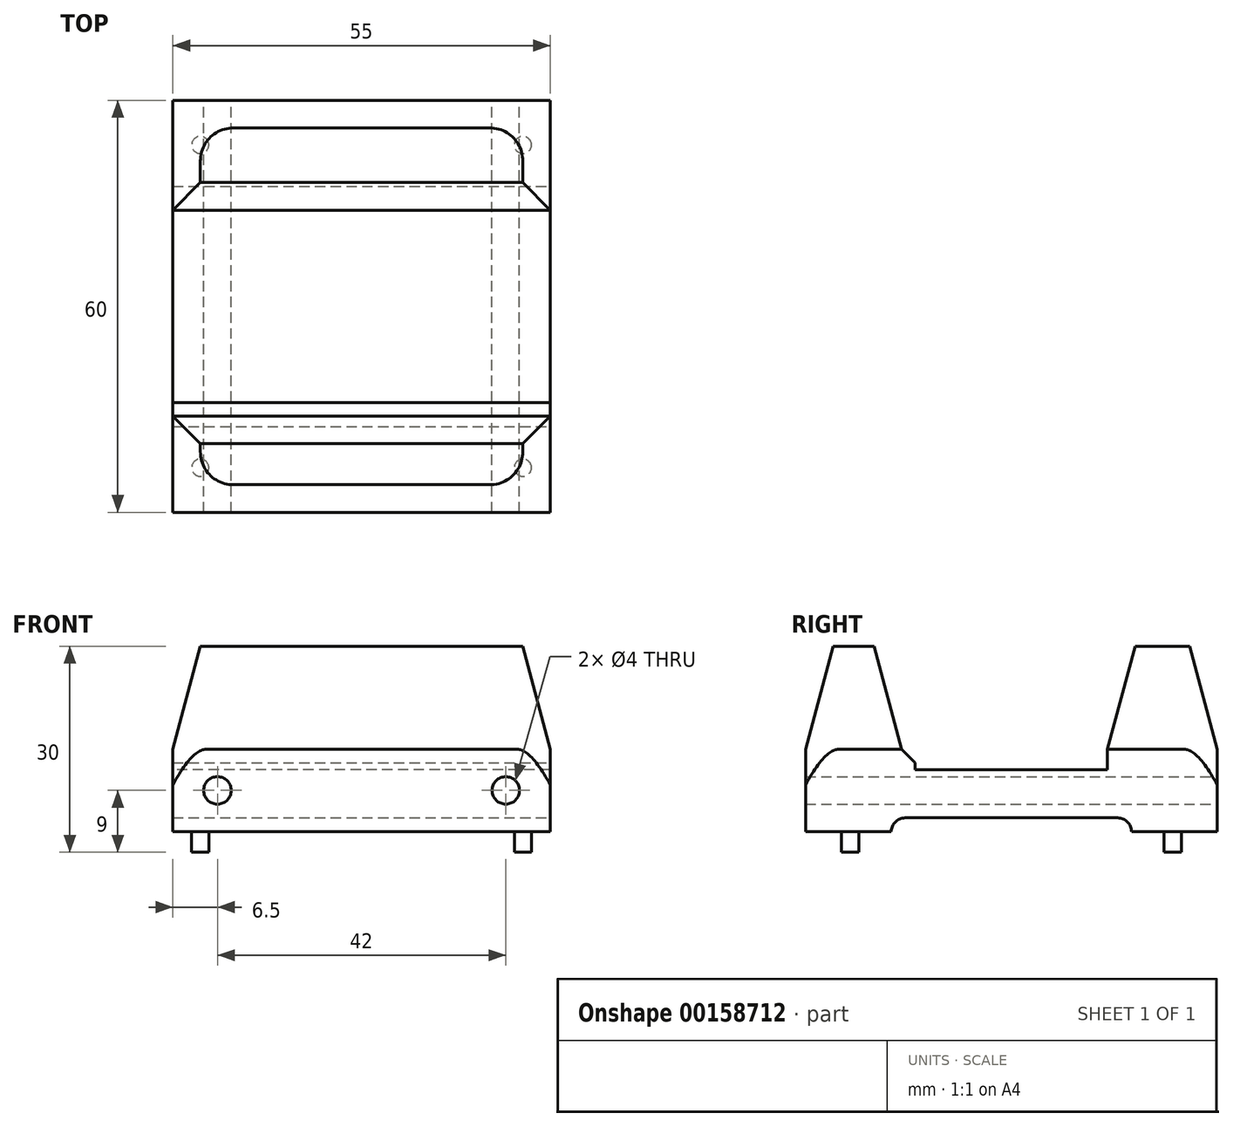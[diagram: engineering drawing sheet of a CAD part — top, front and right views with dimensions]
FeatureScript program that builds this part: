
annotation { "Feature Type Name" : "Feature", "Feature Type Description" : "" }
export const myFeature = defineFeature(function(context is Context, id is Id, definition is map)
    precondition{}
    {
        {
            var Q0;
            Q0=qCreatedBy(makeId("Top.planeOp"),FACE);
            var sketch = newSketch(context, id + "F0", { "sketchPlane" : qUnion([Q0])});
            skLineSegment(sketch, "E0.bottom", {"start": v(-23.5, 23.5) * mm, "end": v(23.5, 23.5) * mm});
            skLineSegment(sketch, "E0.top", {"start": v(-23.5, -23.5) * mm, "end": v(23.5, -23.5) * mm});
            skLineSegment(sketch, "E0.left", {"start": v(-23.5, 23.5) * mm, "end": v(-23.5, -23.5) * mm});
            skLineSegment(sketch, "E0.right", {"start": v(23.5, 23.5) * mm, "end": v(23.5, -23.5) * mm});
            skLineSegment(sketch, "E1", {"start": v(-23.5, 23.5) * mm, "end": v(23.5, -23.5) * mm, "construction": true});
            skLineSegment(sketch, "E2", {"start": v(-23.5, -23.5) * mm, "end": v(23.5, 23.5) * mm, "construction": true});
            skCircle(sketch, "E3", {"center": v(23.5, 23.5) * mm, "radius": 1.25 * mm});
            skCircle(sketch, "E4", {"center": v(23.5, -23.5) * mm, "radius": 1.25 * mm});
            skCircle(sketch, "E5", {"center": v(-23.5, -23.5) * mm, "radius": 1.25 * mm});
            skCircle(sketch, "E6", {"center": v(-23.5, 23.5) * mm, "radius": 1.25 * mm});
            skLineSegment(sketch, "E7.bottom", {"start": v(-27.5, 30) * mm, "end": v(27.5, 30) * mm});
            skLineSegment(sketch, "E7.top", {"start": v(-27.5, -30) * mm, "end": v(27.5, -30) * mm});
            skLineSegment(sketch, "E7.left", {"start": v(-27.5, 30) * mm, "end": v(-27.5, -30) * mm});
            skLineSegment(sketch, "E7.right", {"start": v(27.5, 30) * mm, "end": v(27.5, -30) * mm});
            skSolve(sketch);
        }
        {
            var Q0;
            Q0 = qSketchRegion(id + "F0", true);
            var Q1;
            {var subQ5=sQuery(id+"F0.wireOp",EDGE,"E6");var subQ13=sQuery(id+"F0.wireOp",EDGE,"E0.bottom");var subQ14=makeQuery(id+"F0.imprint","INTERSECT",VERTEX,{"derivedFrom":[subQ13,subQ5]});Q1=makeQuery(id+"F0.imprint","IMPRINT",FACE,{"disambiguationData":[TD([[makeQuery(id+"F0.imprint","IMPRINT",EDGE,{"disambiguationData":[TD([[subQ14,-1.0]])],"derivedFrom":subQ13}),-1.0]])]});}
            var Q2;
            {var subQ0=sQuery(id+"F0.wireOp",EDGE,"E0.left");var subQ1=sQuery(id+"F0.wireOp",EDGE,"E0.bottom");var subQ2=makeQuery(id+"F0.imprint","INTERSECT",VERTEX,{"derivedFrom":[subQ1,subQ0]});Q2=makeQuery(id+"F0.imprint","IMPRINT",FACE,{"disambiguationData":[TD([[makeQuery(id+"F0.imprint","IMPRINT",EDGE,{"disambiguationData":[TD([[subQ2,-1.0]])],"derivedFrom":subQ1}),1.0]])]});}
            var Q3;
            {var subQ0=sQuery(id+"F0.wireOp",EDGE,"E0.left");var subQ1=sQuery(id+"F0.wireOp",EDGE,"E0.bottom");var subQ2=makeQuery(id+"F0.imprint","INTERSECT",VERTEX,{"derivedFrom":[subQ1,subQ0]});Q3=makeQuery(id+"F0.imprint","IMPRINT",FACE,{"disambiguationData":[TD([[makeQuery(id+"F0.imprint","IMPRINT",EDGE,{"disambiguationData":[TD([[subQ2,-1.0]])],"derivedFrom":subQ1}),-1.0]])]});}
            var Q4;
            {var subQ0=sQuery(id+"F0.wireOp",EDGE,"E0.right");var subQ1=sQuery(id+"F0.wireOp",EDGE,"E0.bottom");var subQ2=makeQuery(id+"F0.imprint","INTERSECT",VERTEX,{"derivedFrom":[subQ1,subQ0]});Q4=makeQuery(id+"F0.imprint","IMPRINT",FACE,{"disambiguationData":[TD([[makeQuery(id+"F0.imprint","IMPRINT",EDGE,{"disambiguationData":[TD([[subQ2,1.0]])],"derivedFrom":subQ1}),1.0]])]});}
            var Q5;
            {var subQ0=sQuery(id+"F0.wireOp",EDGE,"E0.right");var subQ1=sQuery(id+"F0.wireOp",EDGE,"E0.bottom");var subQ2=makeQuery(id+"F0.imprint","INTERSECT",VERTEX,{"derivedFrom":[subQ1,subQ0]});Q5=makeQuery(id+"F0.imprint","IMPRINT",FACE,{"disambiguationData":[TD([[makeQuery(id+"F0.imprint","IMPRINT",EDGE,{"disambiguationData":[TD([[subQ2,1.0]])],"derivedFrom":subQ1}),-1.0]])]});}
            var Q6;
            {var subQ0=sQuery(id+"F0.wireOp",EDGE,"E0.right");var subQ1=sQuery(id+"F0.wireOp",EDGE,"E0.top");var subQ2=makeQuery(id+"F0.imprint","INTERSECT",VERTEX,{"derivedFrom":[subQ1,subQ0]});Q6=makeQuery(id+"F0.imprint","IMPRINT",FACE,{"disambiguationData":[TD([[makeQuery(id+"F0.imprint","IMPRINT",EDGE,{"disambiguationData":[TD([[subQ2,1.0]])],"derivedFrom":subQ1}),-1.0]])]});}
            var Q7;
            {var subQ0=sQuery(id+"F0.wireOp",EDGE,"E0.right");var subQ1=sQuery(id+"F0.wireOp",EDGE,"E0.top");var subQ2=makeQuery(id+"F0.imprint","INTERSECT",VERTEX,{"derivedFrom":[subQ1,subQ0]});Q7=makeQuery(id+"F0.imprint","IMPRINT",FACE,{"disambiguationData":[TD([[makeQuery(id+"F0.imprint","IMPRINT",EDGE,{"disambiguationData":[TD([[subQ2,1.0]])],"derivedFrom":subQ1}),1.0]])]});}
            var Q8;
            {var subQ0=sQuery(id+"F0.wireOp",EDGE,"E0.left");var subQ1=sQuery(id+"F0.wireOp",EDGE,"E0.top");var subQ2=makeQuery(id+"F0.imprint","INTERSECT",VERTEX,{"derivedFrom":[subQ1,subQ0]});Q8=makeQuery(id+"F0.imprint","IMPRINT",FACE,{"disambiguationData":[TD([[makeQuery(id+"F0.imprint","IMPRINT",EDGE,{"disambiguationData":[TD([[subQ2,-1.0]])],"derivedFrom":subQ1}),-1.0]])]});}
            var Q9;
            {var subQ0=sQuery(id+"F0.wireOp",EDGE,"E0.left");var subQ1=sQuery(id+"F0.wireOp",EDGE,"E0.top");var subQ2=makeQuery(id+"F0.imprint","INTERSECT",VERTEX,{"derivedFrom":[subQ1,subQ0]});Q9=makeQuery(id+"F0.imprint","IMPRINT",FACE,{"disambiguationData":[TD([[makeQuery(id+"F0.imprint","IMPRINT",EDGE,{"disambiguationData":[TD([[subQ2,-1.0]])],"derivedFrom":subQ1}),1.0]])]});}
            extrude(context, id + "F1", {"entities" : qUnion([Q0, Q1, Q2, Q3, Q4, Q5, Q6, Q7, Q8, Q9]), "depth" : 12 * mm});
        }
        {
            var Q0;
            {var subQ0=sQuery(id+"F0.wireOp",EDGE,"E0.left");var subQ1=sQuery(id+"F0.wireOp",EDGE,"E0.bottom");var subQ2=makeQuery(id+"F0.imprint","INTERSECT",VERTEX,{"derivedFrom":[subQ1,subQ0]});Q0=makeQuery(id+"F0.imprint","IMPRINT",FACE,{"disambiguationData":[TD([[makeQuery(id+"F0.imprint","IMPRINT",EDGE,{"disambiguationData":[TD([[subQ2,-1.0]])],"derivedFrom":subQ1}),1.0]])]});}
            var Q1;
            {var subQ0=sQuery(id+"F0.wireOp",EDGE,"E0.left");var subQ1=sQuery(id+"F0.wireOp",EDGE,"E0.bottom");var subQ2=makeQuery(id+"F0.imprint","INTERSECT",VERTEX,{"derivedFrom":[subQ1,subQ0]});Q1=makeQuery(id+"F0.imprint","IMPRINT",FACE,{"disambiguationData":[TD([[makeQuery(id+"F0.imprint","IMPRINT",EDGE,{"disambiguationData":[TD([[subQ2,-1.0]])],"derivedFrom":subQ1}),-1.0]])]});}
            var Q2;
            {var subQ0=sQuery(id+"F0.wireOp",EDGE,"E0.left");var subQ1=sQuery(id+"F0.wireOp",EDGE,"E0.top");var subQ2=makeQuery(id+"F0.imprint","INTERSECT",VERTEX,{"derivedFrom":[subQ1,subQ0]});Q2=makeQuery(id+"F0.imprint","IMPRINT",FACE,{"disambiguationData":[TD([[makeQuery(id+"F0.imprint","IMPRINT",EDGE,{"disambiguationData":[TD([[subQ2,-1.0]])],"derivedFrom":subQ1}),-1.0]])]});}
            var Q3;
            {var subQ0=sQuery(id+"F0.wireOp",EDGE,"E0.left");var subQ1=sQuery(id+"F0.wireOp",EDGE,"E0.top");var subQ2=makeQuery(id+"F0.imprint","INTERSECT",VERTEX,{"derivedFrom":[subQ1,subQ0]});Q3=makeQuery(id+"F0.imprint","IMPRINT",FACE,{"disambiguationData":[TD([[makeQuery(id+"F0.imprint","IMPRINT",EDGE,{"disambiguationData":[TD([[subQ2,-1.0]])],"derivedFrom":subQ1}),1.0]])]});}
            var Q4;
            {var subQ0=sQuery(id+"F0.wireOp",EDGE,"E0.right");var subQ1=sQuery(id+"F0.wireOp",EDGE,"E0.top");var subQ2=makeQuery(id+"F0.imprint","INTERSECT",VERTEX,{"derivedFrom":[subQ1,subQ0]});Q4=makeQuery(id+"F0.imprint","IMPRINT",FACE,{"disambiguationData":[TD([[makeQuery(id+"F0.imprint","IMPRINT",EDGE,{"disambiguationData":[TD([[subQ2,1.0]])],"derivedFrom":subQ1}),-1.0]])]});}
            var Q5;
            {var subQ0=sQuery(id+"F0.wireOp",EDGE,"E0.right");var subQ1=sQuery(id+"F0.wireOp",EDGE,"E0.top");var subQ2=makeQuery(id+"F0.imprint","INTERSECT",VERTEX,{"derivedFrom":[subQ1,subQ0]});Q5=makeQuery(id+"F0.imprint","IMPRINT",FACE,{"disambiguationData":[TD([[makeQuery(id+"F0.imprint","IMPRINT",EDGE,{"disambiguationData":[TD([[subQ2,1.0]])],"derivedFrom":subQ1}),1.0]])]});}
            var Q6;
            {var subQ0=sQuery(id+"F0.wireOp",EDGE,"E0.right");var subQ1=sQuery(id+"F0.wireOp",EDGE,"E0.bottom");var subQ2=makeQuery(id+"F0.imprint","INTERSECT",VERTEX,{"derivedFrom":[subQ1,subQ0]});Q6=makeQuery(id+"F0.imprint","IMPRINT",FACE,{"disambiguationData":[TD([[makeQuery(id+"F0.imprint","IMPRINT",EDGE,{"disambiguationData":[TD([[subQ2,1.0]])],"derivedFrom":subQ1}),1.0]])]});}
            var Q7;
            {var subQ0=sQuery(id+"F0.wireOp",EDGE,"E0.right");var subQ1=sQuery(id+"F0.wireOp",EDGE,"E0.bottom");var subQ2=makeQuery(id+"F0.imprint","INTERSECT",VERTEX,{"derivedFrom":[subQ1,subQ0]});Q7=makeQuery(id+"F0.imprint","IMPRINT",FACE,{"disambiguationData":[TD([[makeQuery(id+"F0.imprint","IMPRINT",EDGE,{"disambiguationData":[TD([[subQ2,1.0]])],"derivedFrom":subQ1}),-1.0]])]});}
            extrude(context, id + "F2", {"entities" : qUnion([Q0, Q1, Q2, Q3, Q4, Q5, Q6, Q7]), "operationType" : NewBodyOperationType.ADD, "oppositeDirection" : true, "depth" : 3 * mm});
        }
        {
            var Q0;
            Q0=makeQuery(id+"F1.opExtrude","SWEPT_FACE",FACE,{"disambiguationData":[OSD([sQuery(id+"F0.wireOp",EDGE,"E7.right")])]});
            var sketch = newSketch(context, id + "F3", { "sketchPlane" : qUnion([Q0])});
            skLineSegment(sketch, "E8.bottom", {"start": v(-17.5, 0) * mm, "end": v(17.5, 0) * mm});
            skLineSegment(sketch, "E8.top", {"start": v(-17.5, 2) * mm, "end": v(17.5, 2) * mm});
            skLineSegment(sketch, "E8.left", {"start": v(-17.5, 0) * mm, "end": v(-17.5, 2) * mm});
            skLineSegment(sketch, "E8.right", {"start": v(17.5, 0) * mm, "end": v(17.5, 2) * mm});
            skSolve(sketch);
        }
        {
            var Q0;
            Q0=makeQuery(id+"F3.imprint","IMPRINT",FACE,{"disambiguationData":[TD([[makeQuery(id+"F3.imprint","IMPRINT",EDGE,{"derivedFrom":sQuery(id+"F3.wireOp",EDGE,"E8.bottom")}),-1.0]])]});
            extrude(context, id + "F4", {"entities" : qUnion([Q0]), "operationType" : NewBodyOperationType.REMOVE, "oppositeDirection" : true, "depth" : 56.75 * mm});
        }
        {
            var Q0;
            Q0=makeQuery(id+"F4.boolean.opBoolean","COPY",EDGE,{"derivedFrom":makeQuery(id+"F4.opExtrude","SWEPT_EDGE",EDGE,{"disambiguationData":[OSD([sQuery(id+"F3.wireOp",EDGE,"E8.top"),sQuery(id+"F3.wireOp",EDGE,"E8.left")])]})});
            var Q1;
            Q1=makeQuery(id+"F4.boolean.opBoolean","COPY",EDGE,{"derivedFrom":makeQuery(id+"F4.opExtrude","SWEPT_EDGE",EDGE,{"disambiguationData":[OSD([sQuery(id+"F3.wireOp",EDGE,"E8.top"),sQuery(id+"F3.wireOp",EDGE,"E8.right")])]})});
            fillet(context, id + "F5", {"entities" : qUnion([Q0, Q1]), "radius" : 2 * mm, "tangentPropagation" : true, "allowEdgeOverflow" : false});
        }
        {
            var Q0;
            Q0=makeQuery(id+"F1.opExtrude","SWEPT_FACE",FACE,{"disambiguationData":[OSD([sQuery(id+"F0.wireOp",EDGE,"E7.bottom")])]});
            var sketch = newSketch(context, id + "F6", { "sketchPlane" : qUnion([Q0])});
            skCircle(sketch, "E9", {"center": v(-21, 6) * mm, "radius": 2 * mm});
            skCircle(sketch, "E10", {"center": v(21, 6) * mm, "radius": 2 * mm});
            skSolve(sketch);
        }
        {
            var Q0;
            Q0 = qSketchRegion(id + "F6", true);
            extrude(context, id + "F7", {"entities" : qUnion([Q0]), "operationType" : NewBodyOperationType.REMOVE, "oppositeDirection" : true, "depth" : 63.75 * mm});
        }
        {
            var Q0;
            Q0=makeQuery(id+"F1.opExtrude","SWEPT_FACE",FACE,{"disambiguationData":[OSD([sQuery(id+"F0.wireOp",EDGE,"E7.left")])]});
            var sketch = newSketch(context, id + "F8", { "sketchPlane" : qUnion([Q0])});
            skLineSegment(sketch, "E11.bottom", {"start": v(-14, 12) * mm, "end": v(14, 12) * mm});
            skLineSegment(sketch, "E11.top", {"start": v(-14, 9) * mm, "end": v(14, 9) * mm});
            skLineSegment(sketch, "E11.left", {"start": v(-14, 12) * mm, "end": v(-14, 9) * mm});
            skLineSegment(sketch, "E11.right", {"start": v(14, 12) * mm, "end": v(14, 9) * mm});
            skSolve(sketch);
        }
        {
            var Q0;
            Q0=makeQuery(id+"F8.imprint","IMPRINT",FACE,{"disambiguationData":[TD([[makeQuery(id+"F8.imprint","IMPRINT",EDGE,{"derivedFrom":sQuery(id+"F8.wireOp",EDGE,"E11.bottom")}),-1.0]])]});
            extrude(context, id + "F9", {"entities" : qUnion([Q0]), "operationType" : NewBodyOperationType.REMOVE, "oppositeDirection" : true, "depth" : 57.25 * mm});
        }
        {
            var Q0;
            Q0=makeQuery(id+"F9.boolean.opBoolean","COPY",EDGE,{"derivedFrom":makeQuery(id+"F9.opExtrude","SWEPT_EDGE",EDGE,{"disambiguationData":[OSD([sQuery(id+"F0.wireOp",EDGE,"E7.left"),sQuery(id+"F8.wireOp",EDGE,"E11.bottom"),sQuery(id+"F8.wireOp",EDGE,"E11.right")])]})});
            var Q1;
            Q1=makeQuery(id+"F9.boolean.opBoolean","COPY",EDGE,{"derivedFrom":makeQuery(id+"F9.opExtrude","SWEPT_EDGE",EDGE,{"disambiguationData":[OSD([sQuery(id+"F0.wireOp",EDGE,"E7.left"),sQuery(id+"F8.wireOp",EDGE,"E11.bottom"),sQuery(id+"F8.wireOp",EDGE,"E11.left")])]})});
            chamfer(context, id + "F10", {"entities" : qUnion([Q0, Q1]), "width" : 2 * mm, "tangentPropagation" : true});
        }
        {
            var Q0;
            {var subQ0=sQuery(id+"F0.wireOp",EDGE,"E7.bottom");var subQ1=sQuery(id+"F0.wireOp",EDGE,"E7.left");var subQ2=sQuery(id+"F0.wireOp",EDGE,"E7.right");Q0=makeQuery(id+"F9.boolean.opBoolean","SPLIT",FACE,{"disambiguationData":[TD([makeQuery(id+"F1.opExtrude","SWEPT_FACE",FACE,{"disambiguationData":[OSD([subQ0])]})])],"derivedFrom":makeQuery(id+"F1.opExtrude","CAP_FACE",FACE,{"disambiguationData":[OSD([subQ0,sQuery(id+"F0.wireOp",EDGE,"E7.top"),subQ1,subQ2])],"isStart":false})});}
            var Q1;
            {var subQ0=sQuery(id+"F0.wireOp",EDGE,"E7.top");var subQ1=sQuery(id+"F0.wireOp",EDGE,"E7.left");var subQ2=sQuery(id+"F0.wireOp",EDGE,"E7.right");Q1=makeQuery(id+"F9.boolean.opBoolean","SPLIT",FACE,{"disambiguationData":[TD([makeQuery(id+"F1.opExtrude","SWEPT_FACE",FACE,{"disambiguationData":[OSD([subQ0])]})])],"derivedFrom":makeQuery(id+"F1.opExtrude","CAP_FACE",FACE,{"disambiguationData":[OSD([sQuery(id+"F0.wireOp",EDGE,"E7.bottom"),subQ0,subQ1,subQ2])],"isStart":false})});}
            extrude(context, id + "F11", {"entities" : qUnion([Q0, Q1]), "operationType" : NewBodyOperationType.ADD, "depth" : 15 * mm, "hasDraft" : true, "draftAngle" : 15 * degree, "draftPullDirection" : true});
        }
        {
            var Q0;
            Q0=makeQuery(id+"F11.opExtrude","SWEPT_EDGE",EDGE,{"disambiguationData":[OSD([sQuery(id+"F0.wireOp",EDGE,"E7.bottom"),sQuery(id+"F0.wireOp",EDGE,"E7.left")])]});
            var Q1;
            Q1=makeQuery(id+"F11.opExtrude","SWEPT_EDGE",EDGE,{"disambiguationData":[OSD([sQuery(id+"F0.wireOp",EDGE,"E7.bottom"),sQuery(id+"F0.wireOp",EDGE,"E7.right")])]});
            var Q2;
            Q2=makeQuery(id+"F11.opExtrude","SWEPT_EDGE",EDGE,{"disambiguationData":[OSD([sQuery(id+"F0.wireOp",EDGE,"E7.top"),sQuery(id+"F0.wireOp",EDGE,"E7.left")])]});
            var Q3;
            Q3=makeQuery(id+"F11.opExtrude","SWEPT_EDGE",EDGE,{"disambiguationData":[OSD([sQuery(id+"F0.wireOp",EDGE,"E7.top"),sQuery(id+"F0.wireOp",EDGE,"E7.right")])]});
            fillet(context, id + "F12", {"entities" : qUnion([Q0, Q1, Q2, Q3]), "radius" : 5 * mm, "tangentPropagation" : true, "allowEdgeOverflow" : false});
        }
    });
